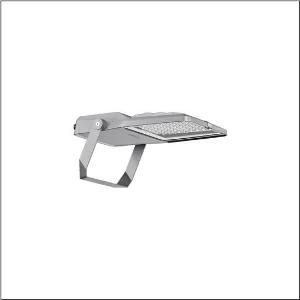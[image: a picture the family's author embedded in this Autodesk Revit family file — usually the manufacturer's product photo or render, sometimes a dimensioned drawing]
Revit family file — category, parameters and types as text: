
# Revit family: floodlight_fl_21_mini___pl61_5xa7776c2c1a_8570
name_source: partatom
category: Lighting Fixtures
units: mm (PartAtom-declared; Revit-internal decimal feet)

## family parameters
Cut with Voids When Loaded = No
Host = Face
Light Source = No
Part Type = Normal
Room Calculation Point = No
Round Connector Dimension = Use Diameter
Shared = No

## types (1)
- --- (1 x LED, 11960 lm, 89 W, 3000K)
    Apparent Load = 89 VA
    CIE Flux Codes = 33 65 98 100 100
    Color Rendering = 70
    Color Temperature = 3000K
    Default Elevation = 1800 mm
    Description = Floodlight FL 21 mini, floodlight, primary light control with lens, of PMMA, primary optical cover: protective disc, of toughened safety glass, transparent, light distribution: PL61, light emission: direct distribution, installation type: surface-mounted, LED, High Power LED, rated luminous flux: 11.960lm, luminous efficacy: 134lm/W, light colour: 730, colour temperature: 3000K, control: flexible luminous flux parameterisation, time-dependent luminous flux control, constant luminous flux control, overheat protection, presetting dimming logarithmic, with terminal, 6-pole, mains connection: 220..240V, AC, 50/60Hz, start of lifetime: 89W, end of service life: 94W, reduction: 43W, luminaire housing, of diecast aluminium, powder-coated, Siteco® metallic grey (DB 702S), corrosivity category C5 mid according to DIN EN ISO 12944, sealing non-destructively replaceable, mounting bracket, of steel, galvanised, powder-coated, Siteco® metallic grey (DB 702S), Smart Interface below and above, protection rating (complete): IP66, insulation class (complete): insulation class II (safety insulation), certification: CE, ENEC, VDE, protection symbol: D, impact resistance: IK08, permissible operating ambient temperature: -40..+40°C, permissible operating ambient temperature for outdoor applications: -40..+50°C, standard: DIN EN 12944, LABS conformity tested according to VDMA 24364:2018-05, packaging unit: 1 piece

Light Distribution: PL61
    Height = 70 mm
    Lamp = 1 x LED
    Lamp Light Flux = 11960 lm
    Lamp Power = 89 W
    Lamp count = 1
    Length = 485 mm
    Luminous efficacy = 134 lm/W
    Manufacturer = Siteco
    ModVariant = No
    Model = 5XA7776C2C1A
    Number of Poles = 1
    OnlyDefault = Yes
    Power Factor = 1
    Product Name = Floodlight FL 21 mini | PL61
    Product group = floodlight | pylon annexe
    ProductGroupID = 6200
    Protection Class = Protection class II
    Protection Degree = IP 66
    RLX_Detail_Level = 1
    RLX_Emergency_Light_Flux = 0 lm
    RLX_Emergency_Type = 0
    RLX_Emergency_Type_DB = No
    RlxData = <blob elided: 95773 chars, md5=a7bfef31>
    Socket = socket
    Standby Power = 0 W
    System Light Flux = 11960 lm
    System Power = 89 W
    Type Comments = factory setting: luminous flux: 100 % | dim-lin: 254 | 456 mA
    Type Image = l_1006845.jpg
    URL = http://relux.com
    VarID = @adj_122957
    Voltage = 0 V
    Weight = 0.00 kg
    Width = 337 mm

## geometry (parser evidence)
native form markers: Blend x4, Sweep x13
no freeform markers — native parametric forms only
